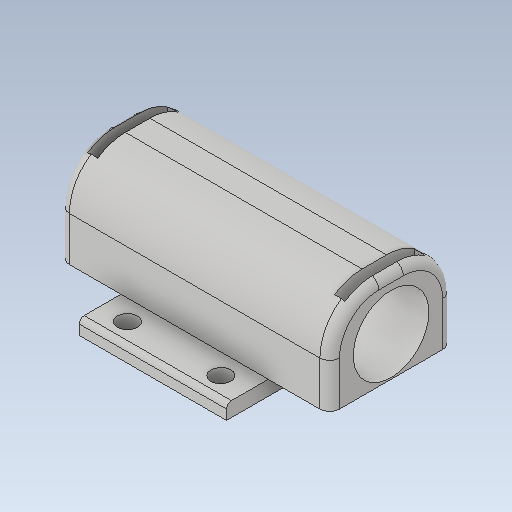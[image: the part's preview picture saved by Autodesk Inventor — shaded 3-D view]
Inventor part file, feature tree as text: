
AUTODESK INVENTOR PART (.ipt)
format: ipt  version: 2020 (Build 240168000, 168)  size: 241,152 bytes
history: native  units: in
note: dims shown in document units (in); Inventor stores cm internally (conversion verified against a paired STEP export)
features: extrude x5, sketch x5, projected_geometry x5, fillet x3, plane x1, mirror x1
ambient origin geometry x8: Origin, YZ Plane, XZ Plane, XY Plane, X Axis, Y Axis, Z Axis, Center Point
bodies: Solid1 (feature_tree)
feature tree (20):
  extrude  "Extrusion1"  Depth=1.6535in
  extrude  "Extrusion2"  Depth=0.75in
  extrude  "Extrusion3"  Depth=0.16in
  fillet  "Fillet1"  Radius=0.16in
  fillet  "Fillet2"  Radius=0.9843in
  fillet  "Fillet3"  Radius=0.748in
  extrude  "Extrusion4"  Depth=2.1654in
  plane  "Work Plane1"
  mirror  "Mirror1"
  extrude  "Extrusion5"  Depth=0.0827in
  sketch  "Sketch1"  dims[d0=1.1811in d1=1.6535in]
  sketch  "Sketch2"  dims[d2=1.313in d3=0.75in]
  sketch  "Sketch3"  dims[d4=0.1181in d5=0.0in d6=0.16in d7=0.16in d9=0.9843in d10=0.748in d11=0.0in]
  projected_geometry  "Projected Loop1"
  projected_geometry  "Projected Loop2"
  sketch  "Sketch4"  dims[d12=0.6063in d13=2.1654in]
  projected_geometry  "Projected Loop3"
  sketch  "Sketch5"  dims[d14=0.9843in d15=0.0in d16=0.9488in d18=0.0827in d20=0.2402in d21=0.0in d26=0.3937in d27=0.0in d28=0.4331in d29=0.3937in d30=0.0787in d31=0.0394in d34=0.3189in d35=0.3189in d36=0.16in d37=0.16in]
  projected_geometry  "Projected Loop4"
  projected_geometry  "Projected Loop5"
